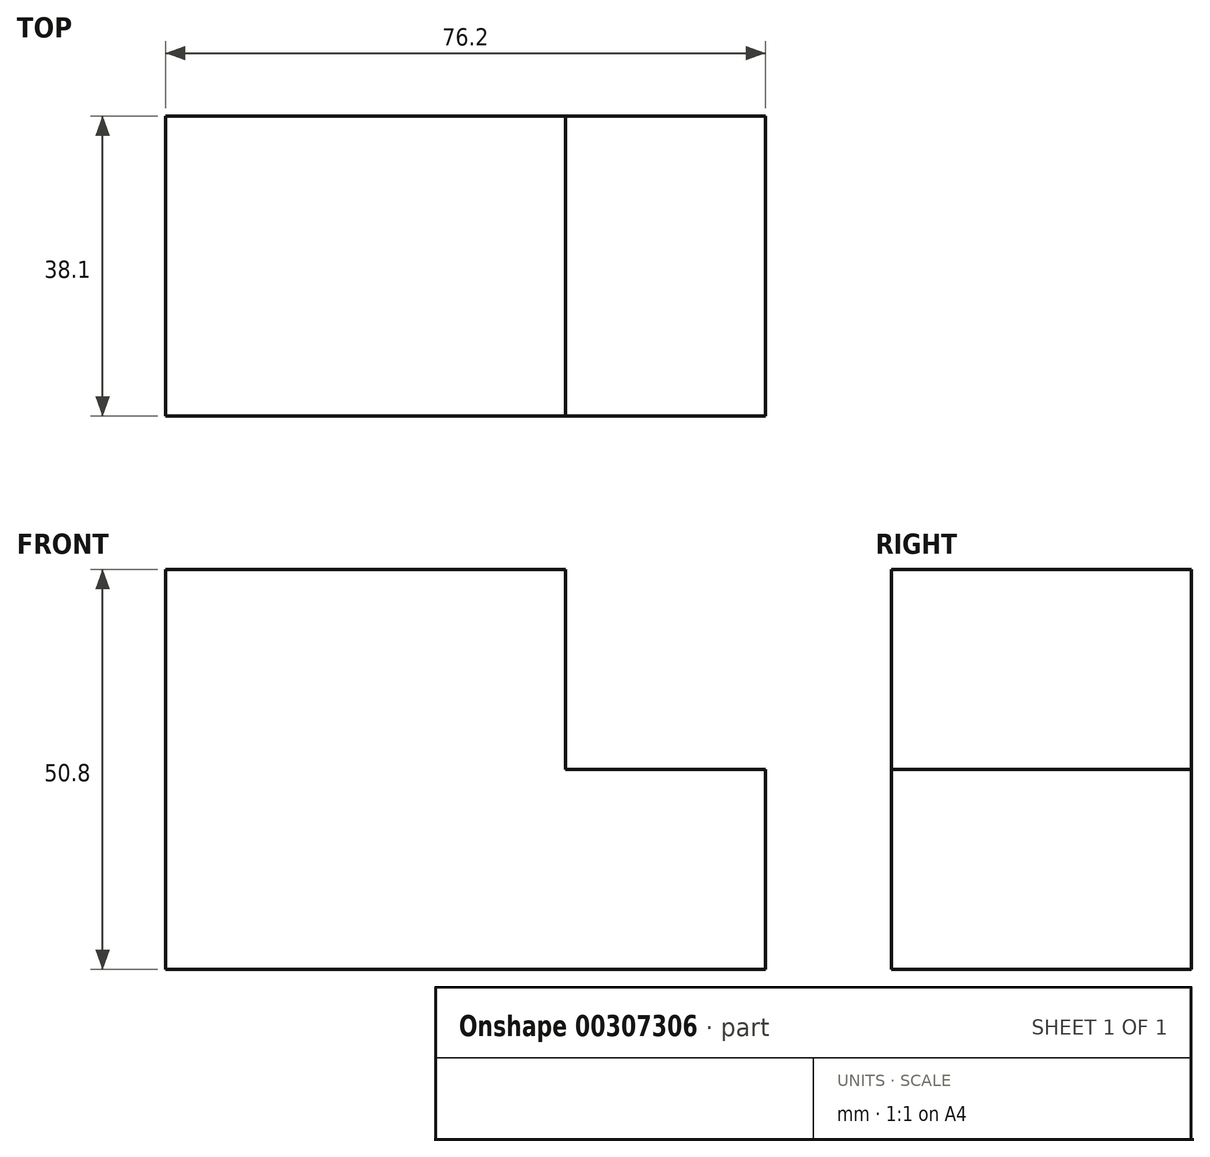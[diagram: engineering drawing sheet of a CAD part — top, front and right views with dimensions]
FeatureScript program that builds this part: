
annotation { "Feature Type Name" : "Feature", "Feature Type Description" : "" }
export const myFeature = defineFeature(function(context is Context, id is Id, definition is map)
    precondition{}
    {
        {
            var Q0;
            Q0=qCreatedBy(makeId("Front.planeOp"),FACE);
            var sketch = newSketch(context, id + "F0", { "sketchPlane" : qUnion([Q0])});
            skLineSegment(sketch, "E0", {"start": v(-38.96, 26.79) * mm, "end": v(-38.96, -24.01) * mm});
            skLineSegment(sketch, "E1", {"start": v(-38.96, -24.01) * mm, "end": v(37.24, -24.01) * mm});
            skLineSegment(sketch, "E2", {"start": v(37.24, -24.01) * mm, "end": v(37.24, 1.39) * mm});
            skLineSegment(sketch, "E3", {"start": v(37.24, 1.39) * mm, "end": v(11.84, 1.39) * mm});
            skLineSegment(sketch, "E4", {"start": v(11.84, 1.39) * mm, "end": v(11.84, 26.79) * mm});
            skLineSegment(sketch, "E5", {"start": v(11.84, 26.79) * mm, "end": v(-38.96, 26.79) * mm});
            skSolve(sketch);
        }
        {
            var Q0;
            Q0=makeQuery(id+"F0.imprint","IMPRINT",FACE,{"disambiguationData":[TD([[makeQuery(id+"F0.imprint","IMPRINT",EDGE,{"derivedFrom":sQuery(id+"F0.wireOp",EDGE,"E0")}),1.0]])]});
            extrude(context, id + "F1", {"entities" : qUnion([Q0]), "depth" : 38.1 * mm});
        }
    });
